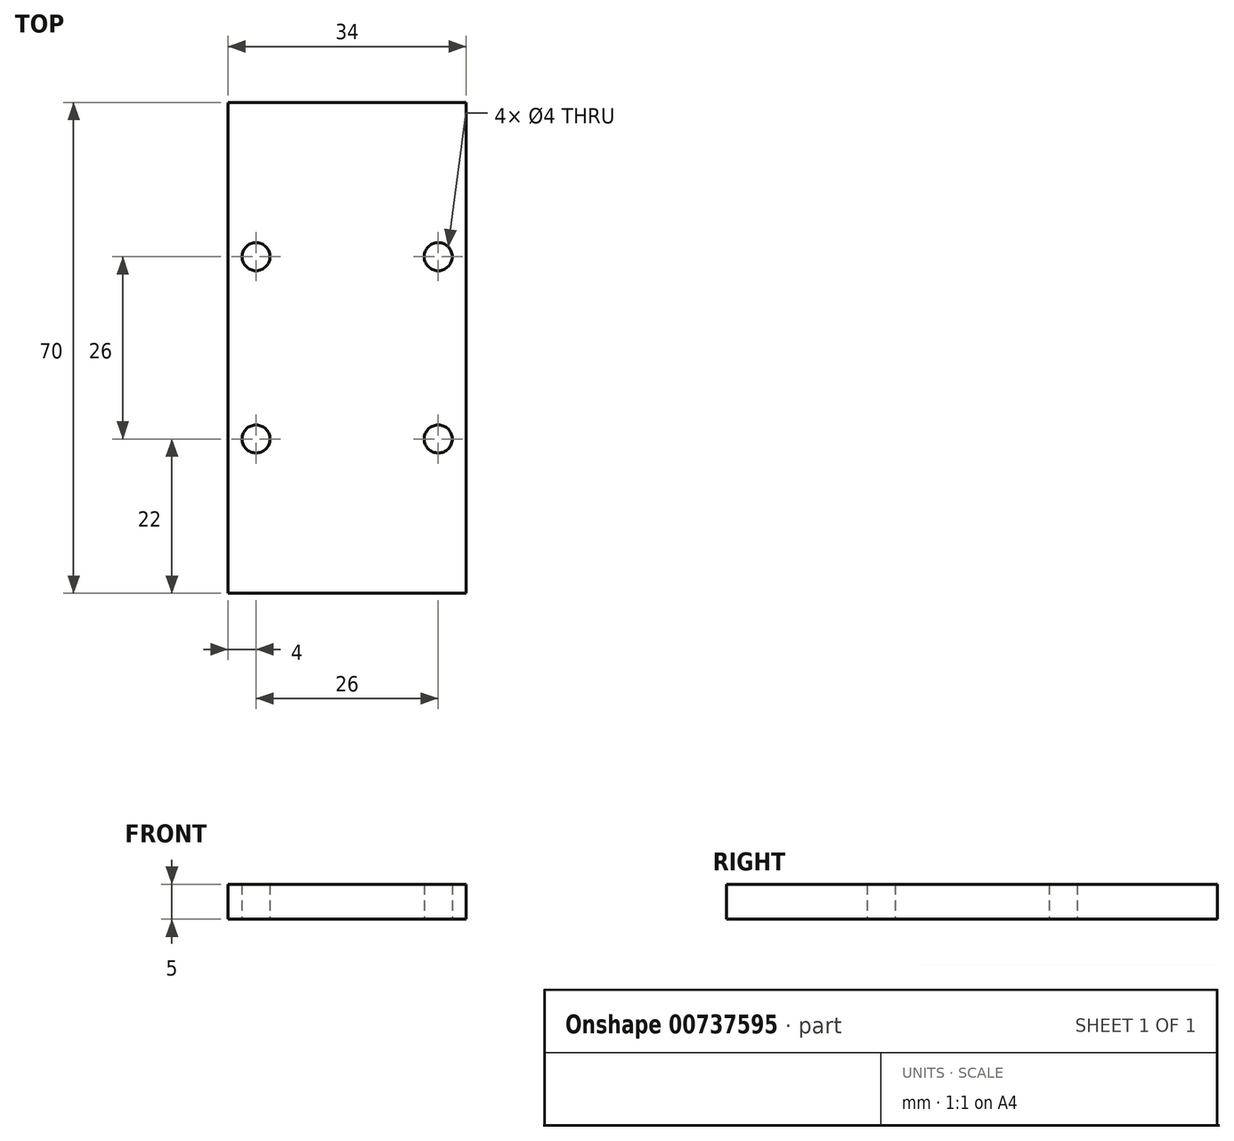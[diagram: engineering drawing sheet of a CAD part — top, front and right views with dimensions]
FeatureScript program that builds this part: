
annotation { "Feature Type Name" : "Feature", "Feature Type Description" : "" }
export const myFeature = defineFeature(function(context is Context, id is Id, definition is map)
    precondition{}
    {
        {
            var Q0;
            Q0=qCreatedBy(makeId("Top.planeOp"),FACE);
            var sketch = newSketch(context, id + "F0", { "sketchPlane" : qUnion([Q0])});
            skLineSegment(sketch, "E0.bottom", {"start": v(-13, 13) * mm, "end": v(13, 13) * mm, "construction": true});
            skLineSegment(sketch, "E0.top", {"start": v(-13, -13) * mm, "end": v(13, -13) * mm, "construction": true});
            skLineSegment(sketch, "E0.left", {"start": v(-13, 13) * mm, "end": v(-13, -13) * mm, "construction": true});
            skLineSegment(sketch, "E0.right", {"start": v(13, 13) * mm, "end": v(13, -13) * mm, "construction": true});
            skPoint(sketch, "E0.middle", {"position": v(0, 0) * mm});
            skCircle(sketch, "E1", {"center": v(-13, 13) * mm, "radius": 2 * mm});
            skCircle(sketch, "E2.MirrorC", {"center": v(13, 13) * mm, "radius": 2 * mm});
            skCircle(sketch, "E3.MirrorC", {"center": v(-13, -13) * mm, "radius": 2 * mm});
            skCircle(sketch, "E4.MirrorC", {"center": v(13, -13) * mm, "radius": 2 * mm});
            skLineSegment(sketch, "E5.bottom", {"start": v(-17, 35) * mm, "end": v(17, 35) * mm});
            skLineSegment(sketch, "E5.top", {"start": v(-17, -35) * mm, "end": v(17, -35) * mm});
            skLineSegment(sketch, "E5.left", {"start": v(-17, 35) * mm, "end": v(-17, -35) * mm});
            skLineSegment(sketch, "E5.right", {"start": v(17, 35) * mm, "end": v(17, -35) * mm});
            skSolve(sketch);
        }
        {
            var Q0;
            Q0=makeQuery(id+"F0.imprint","IMPRINT",FACE,{"disambiguationData":[TD([[makeQuery(id+"F0.imprint","IMPRINT",EDGE,{"derivedFrom":sQuery(id+"F0.wireOp",EDGE,"E1")}),-1.0]])]});
            extrude(context, id + "F1", {"entities" : qUnion([Q0]), "depth" : 5 * mm, "offsetDistance" : 25 * mm});
        }
    });
